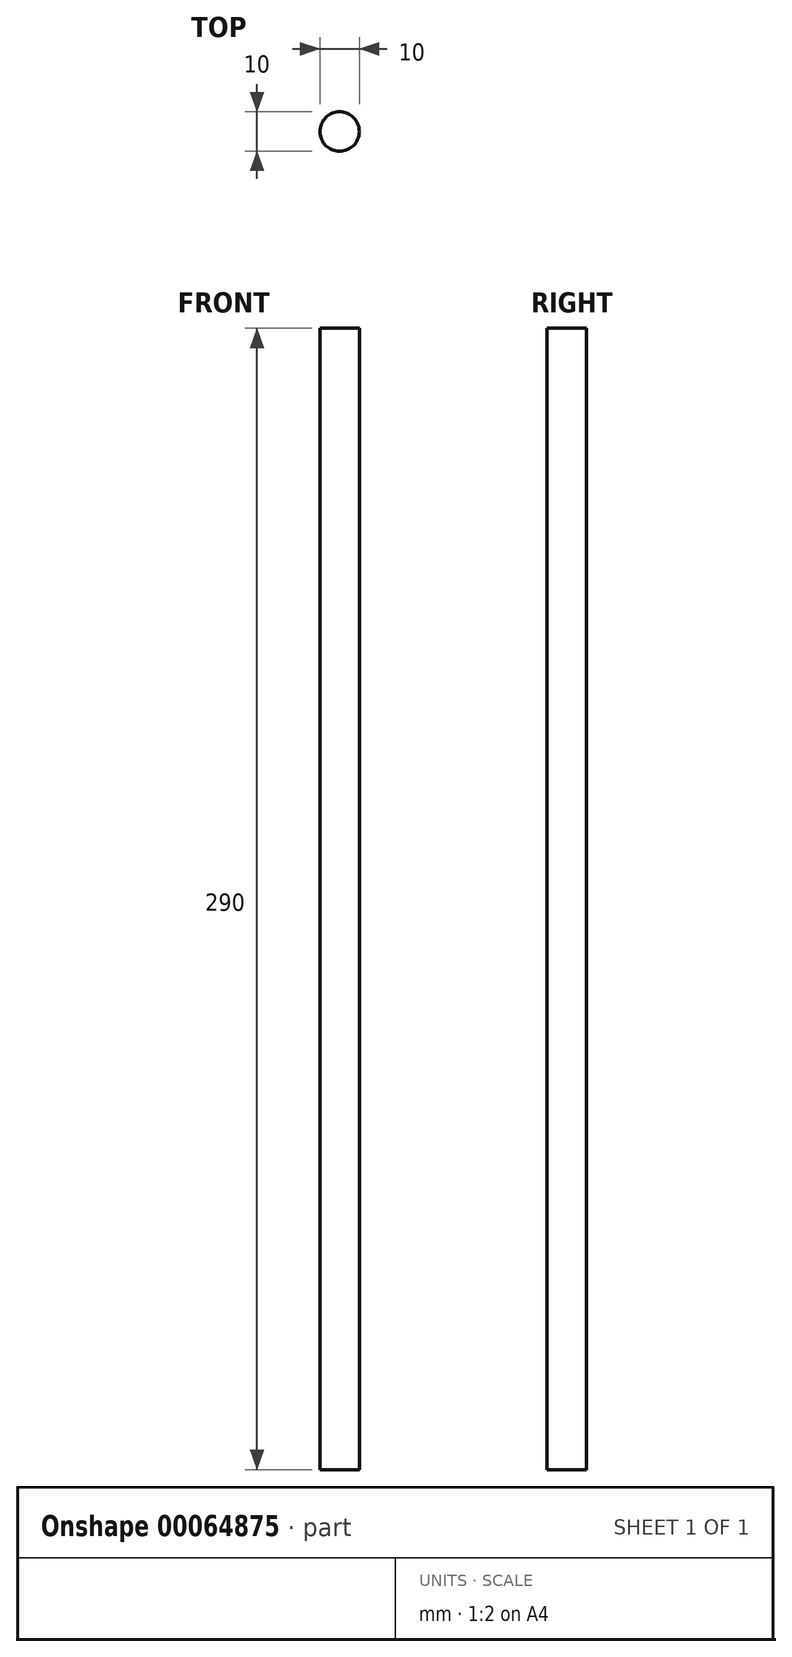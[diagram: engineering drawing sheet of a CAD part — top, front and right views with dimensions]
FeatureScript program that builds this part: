
annotation { "Feature Type Name" : "Feature", "Feature Type Description" : "" }
export const myFeature = defineFeature(function(context is Context, id is Id, definition is map)
    precondition{}
    {
        {
            var Q0;
            Q0=qCreatedBy(makeId("Top.planeOp"),FACE);
            var sketch = newSketch(context, id + "F0", { "sketchPlane" : qUnion([Q0])});
            skCircle(sketch, "E0", {"center": v(0, 0) * mm, "radius": 5 * mm});
            skSolve(sketch);
        }
        {
            var Q0;
            Q0=qSketchRegion(id+"F0",true);
            extrude(context, id + "F1", {"entities" : qUnion([Q0]), "depth" : 290 * mm, "offsetDistance" : 25 * mm});
        }
    });
